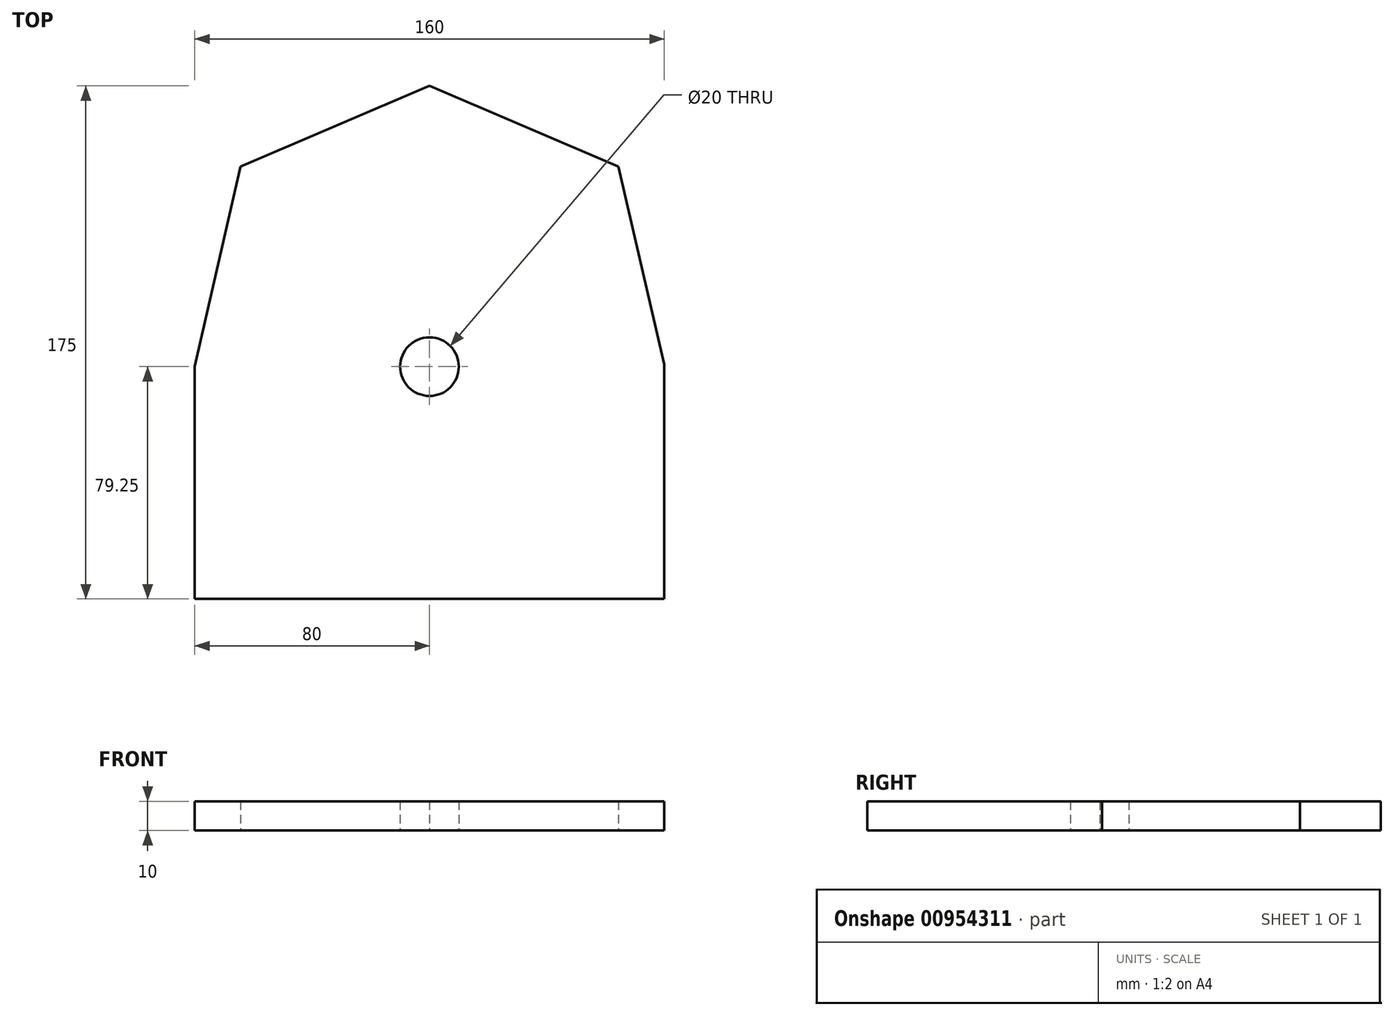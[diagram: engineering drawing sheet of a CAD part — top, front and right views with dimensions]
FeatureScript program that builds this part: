
annotation { "Feature Type Name" : "Feature", "Feature Type Description" : "" }
export const myFeature = defineFeature(function(context is Context, id is Id, definition is map)
    precondition{}
    {
        {
            var Q0;
            Q0=qCreatedBy(makeId("Top.planeOp"),FACE);
            var sketch = newSketch(context, id + "F0", { "sketchPlane" : qUnion([Q0])});
            skLineSegment(sketch, "E0", {"start": v(0, 0) * mm, "end": v(0, 95.75) * mm, "construction": true});
            skLineSegment(sketch, "E1", {"start": v(0, 0) * mm, "end": v(-80, 0) * mm, "construction": true});
            skLineSegment(sketch, "E2.top", {"start": v(-80, -79.25) * mm, "end": v(80, -79.25) * mm});
            skLineSegment(sketch, "E2.left", {"start": v(-80, 0) * mm, "end": v(-80, -79.25) * mm});
            skLineSegment(sketch, "E2.right", {"start": v(80, 0.75) * mm, "end": v(80, -79.25) * mm});
            skLineSegment(sketch, "E3", {"start": v(-80, 0) * mm, "end": v(-64.37, 68.23) * mm});
            skLineSegment(sketch, "E4", {"start": v(-64.37, 68.23) * mm, "end": v(0, 95.75) * mm});
            skLineSegment(sketch, "E5", {"start": v(0, 95.75) * mm, "end": v(64.37, 68.23) * mm});
            skLineSegment(sketch, "E6", {"start": v(64.37, 68.23) * mm, "end": v(80, 0.75) * mm});
            skCircle(sketch, "E7", {"center": v(0, 0) * mm, "radius": 10 * mm});
            skSolve(sketch);
        }
        {
            var Q0;
            Q0=makeQuery(id+"F0.imprint","IMPRINT",FACE,{"disambiguationData":[TD([[makeQuery(id+"F0.imprint","IMPRINT",EDGE,{"derivedFrom":sQuery(id+"F0.wireOp",EDGE,"E2.top")}),1.0]])]});
            extrude(context, id + "F1", {"entities" : qUnion([Q0]), "depth" : 10 * mm, "offsetDistance" : 25 * mm});
        }
    });
